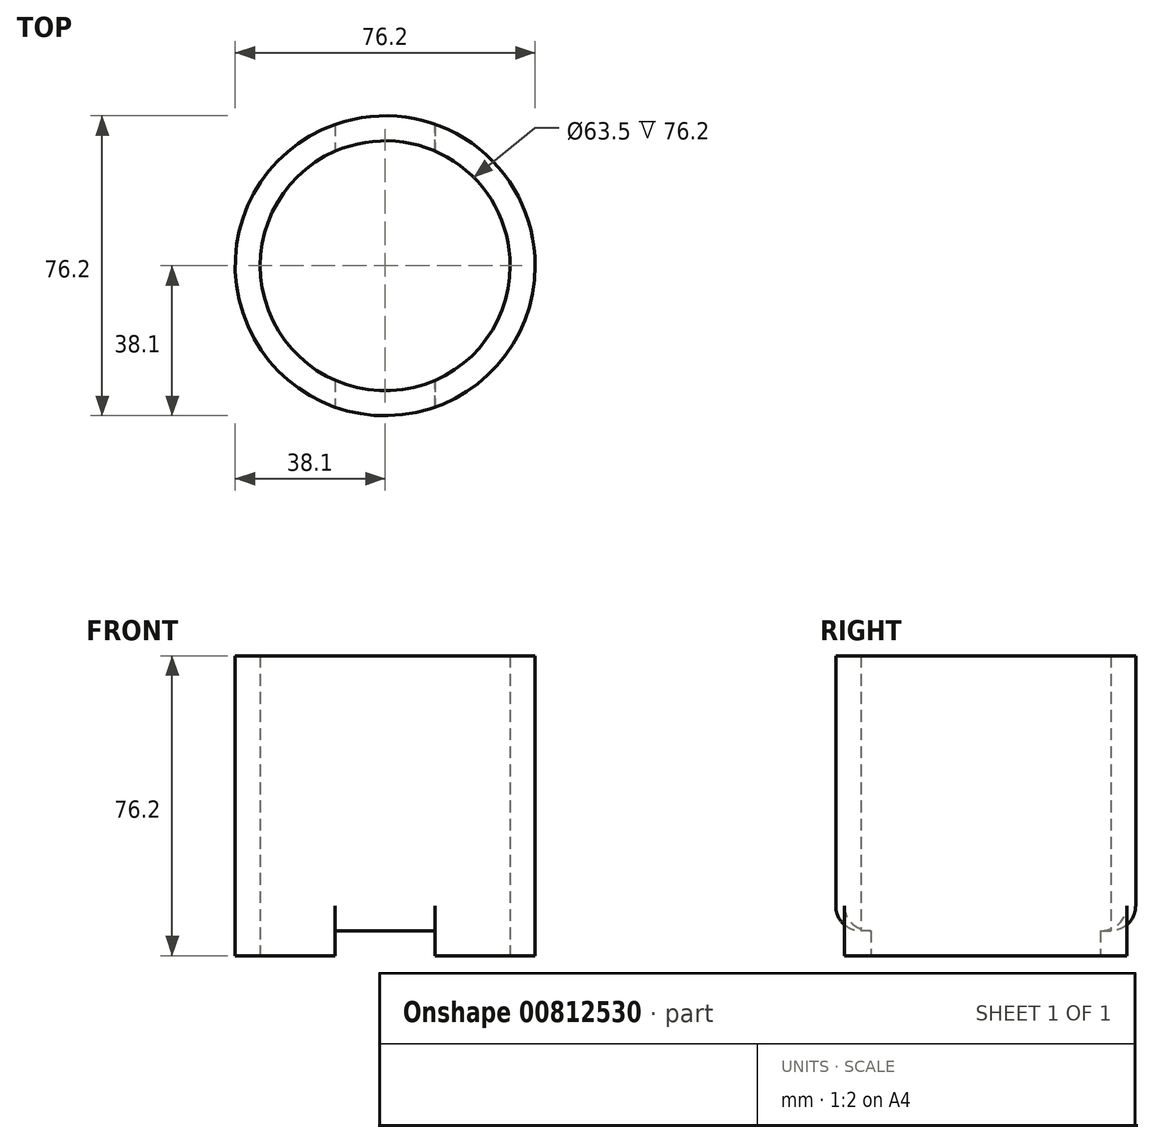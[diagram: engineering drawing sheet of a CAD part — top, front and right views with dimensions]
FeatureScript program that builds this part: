
annotation { "Feature Type Name" : "Feature", "Feature Type Description" : "" }
export const myFeature = defineFeature(function(context is Context, id is Id, definition is map)
    precondition{}
    {
        {
            var Q0;
            Q0=qCreatedBy(makeId("Top.planeOp"),FACE);
            var sketch = newSketch(context, id + "F0", { "sketchPlane" : qUnion([Q0])});
            skCircle(sketch, "E0", {"center": v(0, 0) * mm, "radius": 38.1 * mm});
            skSolve(sketch);
        }
        {
            var Q0;
            Q0=makeQuery(id+"F0.imprint","IMPRINT",FACE,{"disambiguationData":[TD([[makeQuery(id+"F0.imprint","IMPRINT",EDGE,{"derivedFrom":sQuery(id+"F0.wireOp",EDGE,"E0")}),1.0]])]});
            extrude(context, id + "F1", {"entities" : qUnion([Q0]), "depth" : 76.2 * mm, "offsetDistance" : 25.4 * mm});
        }
        {
            var Q0;
            Q0=qCreatedBy(makeId("Front.planeOp"),FACE);
            var sketch = newSketch(context, id + "F2", { "sketchPlane" : qUnion([Q0])});
            skLineSegment(sketch, "E1.bottom", {"start": v(12.7, 6.35) * mm, "end": v(-12.7, 6.35) * mm});
            skLineSegment(sketch, "E1.top", {"start": v(12.7, -6.35) * mm, "end": v(-12.7, -6.35) * mm});
            skLineSegment(sketch, "E1.left", {"start": v(12.7, 6.35) * mm, "end": v(12.7, -6.35) * mm});
            skLineSegment(sketch, "E1.right", {"start": v(-12.7, 6.35) * mm, "end": v(-12.7, -6.35) * mm});
            skPoint(sketch, "E1.middle", {"position": v(0, 0) * mm});
            skSolve(sketch);
        }
        {
            var Q0;
            Q0=makeQuery(id+"F2.imprint","IMPRINT",FACE,{"disambiguationData":[TD([[makeQuery(id+"F2.imprint","IMPRINT",EDGE,{"derivedFrom":sQuery(id+"F2.wireOp",EDGE,"E1.bottom")}),1.0]])]});
            extrude(context, id + "F3", {"entities" : qUnion([Q0]), "operationType" : NewBodyOperationType.REMOVE, "endBound" : BoundingType.SYMMETRIC, "oppositeDirection" : true, "depth" : 127 * mm, "offsetDistance" : 25.4 * mm});
        }
        {
            var Q0;
            Q0=makeQuery(id+"F3.boolean.opBoolean","INTERSECT",EDGE,{"disambiguationData":[OD(0.0)],"derivedFrom":[makeQuery(id+"F1.opExtrude","SWEPT_FACE",FACE,{"disambiguationData":[OSD([sQuery(id+"F0.wireOp",EDGE,"E0")])]}),makeQuery(id+"F3.opExtrude","SWEPT_FACE",FACE,{"disambiguationData":[OSD([sQuery(id+"F2.wireOp",EDGE,"E1.bottom")])]})]});
            var Q1;
            Q1=makeQuery(id+"F3.boolean.opBoolean","INTERSECT",EDGE,{"disambiguationData":[OD(1.0)],"derivedFrom":[makeQuery(id+"F1.opExtrude","SWEPT_FACE",FACE,{"disambiguationData":[OSD([sQuery(id+"F0.wireOp",EDGE,"E0")])]}),makeQuery(id+"F3.opExtrude","SWEPT_FACE",FACE,{"disambiguationData":[OSD([sQuery(id+"F2.wireOp",EDGE,"E1.bottom")])]})]});
            fillet(context, id + "F4", {"entities" : qUnion([Q0, Q1]), "radius" : 6.35 * mm, "tangentPropagation" : true, "allowEdgeOverflow" : false});
        }
        {
            var Q0;
            {var subQ0=sQuery(id+"F0.wireOp",EDGE,"E0");Q0=makeQuery(id+"F3.boolean.opBoolean","SPLIT",FACE,{"disambiguationData":[TD([makeQuery(id+"F3.opExtrude","SWEPT_FACE",FACE,{"disambiguationData":[OSD([sQuery(id+"F2.wireOp",EDGE,"E1.right")])]})])],"derivedFrom":makeQuery(id+"F1.opExtrude","CAP_FACE",FACE,{"disambiguationData":[OSD([subQ0])],"isStart":true})});}
            var sketch = newSketch(context, id + "F5", { "sketchPlane" : qUnion([Q0])});
            skCircle(sketch, "E2", {"center": v(0, 0) * mm, "radius": 31.75 * mm});
            skSolve(sketch);
        }
        {
            var Q0;
            Q0 = qSketchRegion(id + "F5", true);
            extrude(context, id + "F6", {"entities" : qUnion([Q0]), "operationType" : NewBodyOperationType.REMOVE, "endBound" : BoundingType.THROUGH_ALL, "oppositeDirection" : true, "depth" : 25.4 * mm, "offsetDistance" : 25.4 * mm});
        }
    });
